# Revit family: Ekeby Bench - Wall Mounted
name_source: partatom
category: Furniture
units: mm (PartAtom-declared; Revit-internal decimal feet)

## family parameters
Always vertical = Yes
Cut with Voids When Loaded = No
OmniClass Number = 23.21.23.13.15
Room Calculation Point = No
Shared = No
Work Plane-Based = No

## types (2) — shared parameters
BIMobject category = Bench & Park Bench
Body material = Hags - Wood - Bark brown
Body material_90 = Hags - Wood - Bark brown 90
Construction material = Hags - Steel - Galvanized
Description = Ekeby Bench
Edition number = 1
IFC Classification = Furniture
Manufacturer = Hags
Manufacturer name = HAGS
OmniClass Code = 23-21 23 13 15
OmniClass Description = Residential Sofas
Product Guid = 90e49432-c870-4a59-897e-b15016e8f9bd
Product name = Ekeby Bench - Wall Mounted
Product url = https://www.hags.com
QR code = https://www.hags.com
URL = https://www.hags.com
Uniclass 1.4 Code = L8211
Uniclass 1.4 Description = Furniture
zero-valued in all types: Default Elevation

## per-type parameters (varying)
| type | Model |
| 8098806 Dark Brown/ Galvanized | 8098806 |
| 8098581 Dark Brown/ Black | 8098581 |

## geometry (parser evidence)
native form markers: Sweep x3
no freeform markers — native parametric forms only
